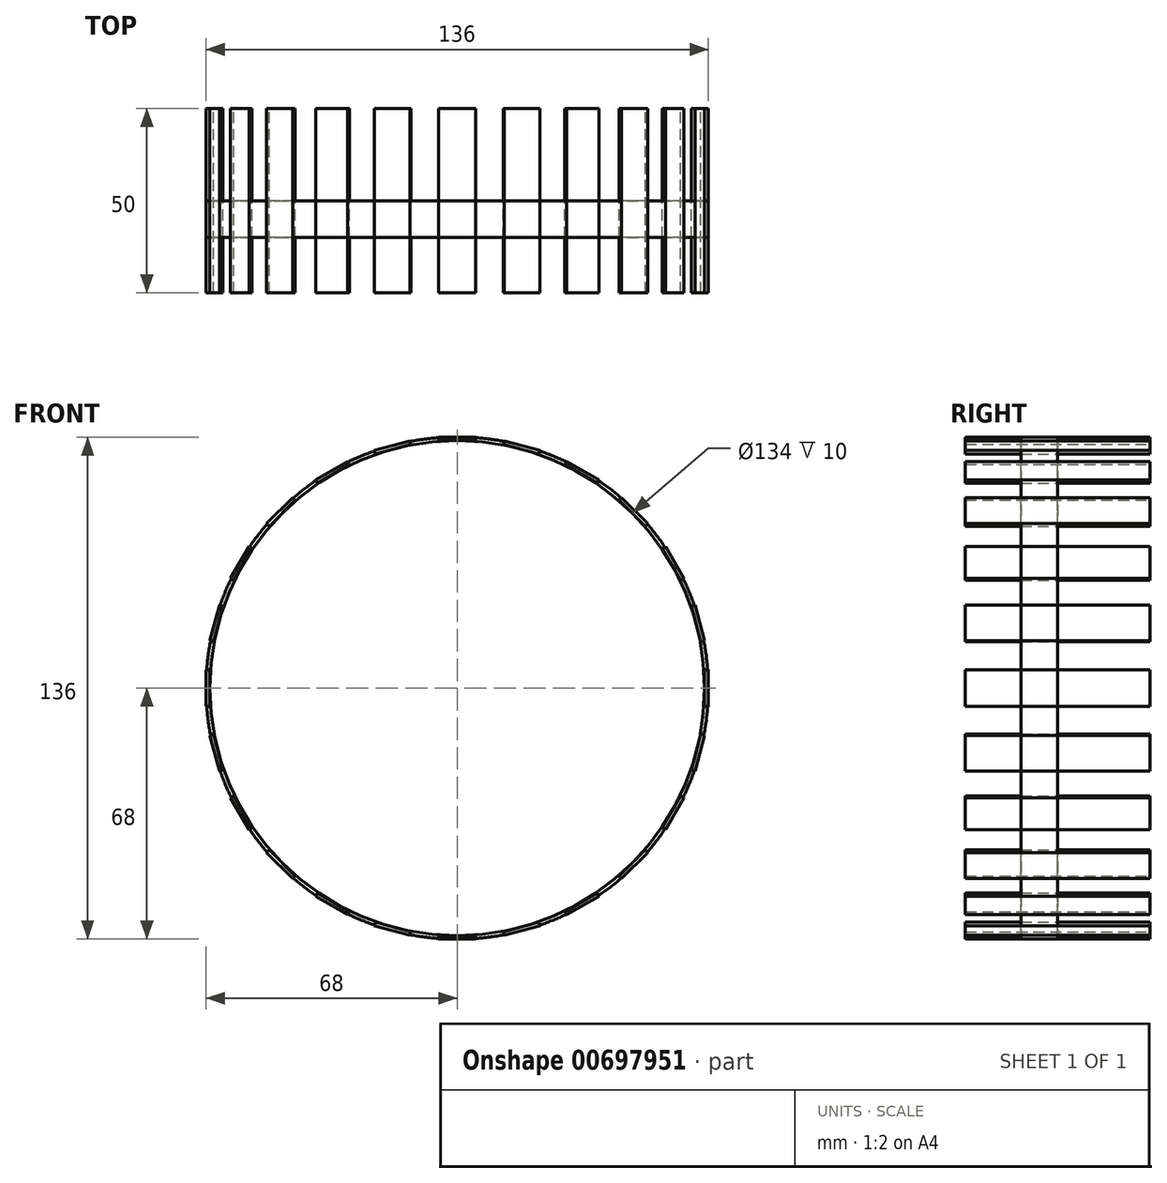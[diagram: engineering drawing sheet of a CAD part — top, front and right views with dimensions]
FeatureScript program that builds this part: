
annotation { "Feature Type Name" : "Feature", "Feature Type Description" : "" }
export const myFeature = defineFeature(function(context is Context, id is Id, definition is map)
    precondition{}
    {
        {
            var Q0;
            Q0=qCreatedBy(makeId("Front.planeOp"),FACE);
            var sketch = newSketch(context, id + "F0", { "sketchPlane" : qUnion([Q0])});
            skCircle(sketch, "E0", {"center": v(0, 0) * mm, "radius": 5 * mm});
            skLineSegment(sketch, "E1", {"start": v(0, 67) * mm, "end": v(-5, 67) * mm});
            skLineSegment(sketch, "E2", {"start": v(-5, 67) * mm, "end": v(-5, 67) * mm});
            skLineSegment(sketch, "E3", {"start": v(-5, 67) * mm, "end": v(-5, 68) * mm});
            skLineSegment(sketch, "E4", {"start": v(-5, 68) * mm, "end": v(5, 68) * mm});
            skLineSegment(sketch, "E5", {"start": v(0, 67) * mm, "end": v(5, 67) * mm});
            skLineSegment(sketch, "E6", {"start": v(5, 68) * mm, "end": v(5, 67) * mm});
            skSolve(sketch);
        }
        {
            var Q0;
            Q0=makeQuery(id+"F0.imprint","IMPRINT",FACE,{"disambiguationData":[TD([[makeQuery(id+"F0.imprint","IMPRINT",EDGE,{"derivedFrom":sQuery(id+"F0.wireOp",EDGE,"E1")}),-1.0]])]});
            var Q1;
            Q1=makeQuery(id+"F0.imprint","IMPRINT",FACE,{"disambiguationData":[TD([[makeQuery(id+"F0.imprint","IMPRINT",EDGE,{"derivedFrom":sQuery(id+"F0.wireOp",EDGE,"E0")}),1.0]])]});
            extrude(context, id + "F1", {"entities" : qUnion([Q0, Q1]), "depth" : 50 * mm, "offsetDistance" : 25 * mm});
        }
        {
            var Q0;
            Q0=makeQuery(id+"F1.opExtrude","SWEPT_BODY",BODY,{"disambiguationData":[OSD([sQuery(id+"F0.wireOp",EDGE,"E1"),sQuery(id+"F0.wireOp",EDGE,"E3"),sQuery(id+"F0.wireOp",EDGE,"E4"),sQuery(id+"F0.wireOp",EDGE,"E5"),sQuery(id+"F0.wireOp",EDGE,"E6")])]});
            var Q1;
            Q1=makeQuery(id+"F1.opExtrude","SWEPT_FACE",FACE,{"disambiguationData":[OSD([sQuery(id+"F0.wireOp",EDGE,"E0")])]});
            circularPattern(context, id + "F2", {"entities" : qUnion([Q0]), "axis" : qUnion([Q1]), "angle" : 360 * degree, "instanceCount" : 24, "equalSpace" : true});
        }
        {
            var Q0;
            Q0=makeQuery(id+"F1.opExtrude","CAP_FACE",FACE,{"disambiguationData":[OSD([sQuery(id+"F0.wireOp",EDGE,"E0")])],"isStart":false});
            extrude(context, id + "F3", {"entities" : qUnion([Q0]), "operationType" : NewBodyOperationType.REMOVE, "oppositeDirection" : true, "depth" : 50 * mm, "offsetDistance" : 25 * mm});
        }
        {
            var Q0;
            Q0=qCreatedBy(makeId("Front.planeOp"),FACE);
            cPlane(context, id + "F4", {"entities" : qUnion([Q0]), "cplaneType" : CPlaneType.OFFSET, "offset" : 25 * mm, "width" : 150 * mm, "height" : 150 * mm});
        }
        {
            var Q0;
            Q0=qCreatedBy(id+"F4.planeOp",FACE);
            var sketch = newSketch(context, id + "F5", { "sketchPlane" : qUnion([Q0])});
            skCircle(sketch, "E7", {"center": v(0, 0) * mm, "radius": 68 * mm});
            skCircle(sketch, "E8", {"center": v(0, 0) * mm, "radius": 67 * mm});
            skSolve(sketch);
        }
        {
            var Q0;
            Q0=makeQuery(id+"F5.imprint","IMPRINT",FACE,{"disambiguationData":[TD([[makeQuery(id+"F5.imprint","IMPRINT",EDGE,{"derivedFrom":sQuery(id+"F5.wireOp",EDGE,"E7")}),1.0]])]});
            extrude(context, id + "F6", {"entities" : qUnion([Q0]), "depth" : 10 * mm, "offsetDistance" : 25 * mm});
        }
    });
